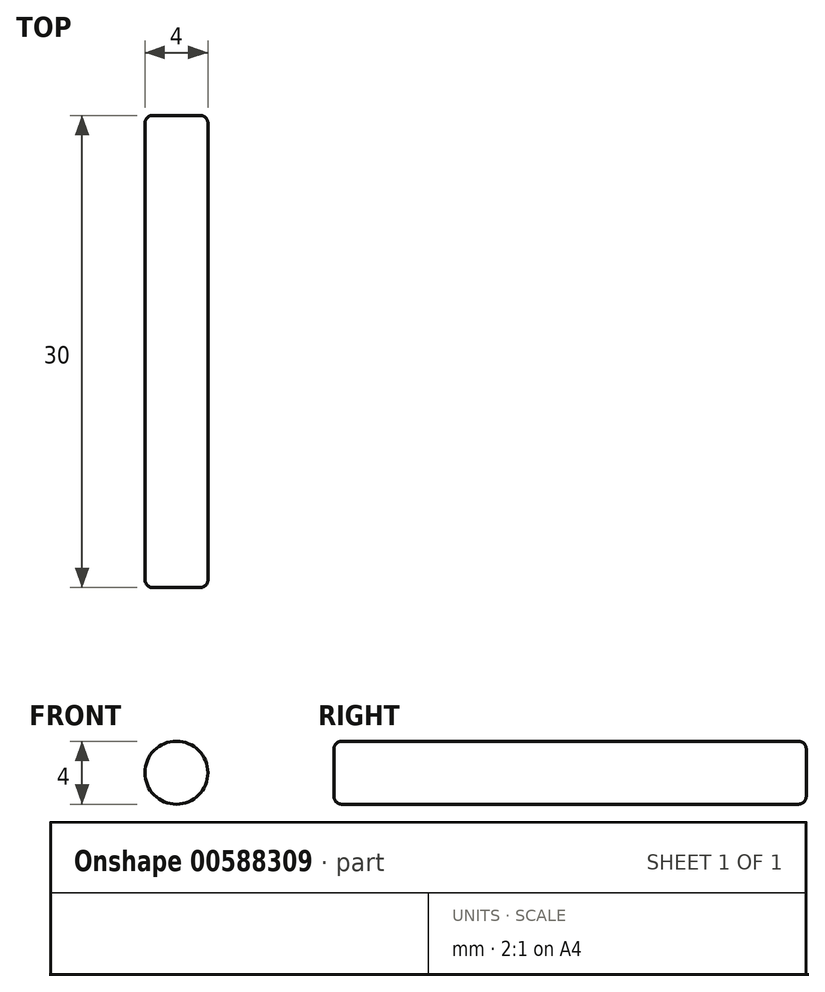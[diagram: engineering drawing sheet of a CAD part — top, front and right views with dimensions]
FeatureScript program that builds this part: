
annotation { "Feature Type Name" : "Feature", "Feature Type Description" : "" }
export const myFeature = defineFeature(function(context is Context, id is Id, definition is map)
    precondition{}
    {
        {
            var Q0;
            Q0=qCreatedBy(makeId("Right.planeOp"),FACE);
            var sketch = newSketch(context, id + "F0", { "sketchPlane" : qUnion([Q0])});
            skLineSegment(sketch, "E0", {"start": v(-95.37, 9.25) * mm, "end": v(-41.61, 9.25) * mm, "construction": true});
            skLineSegment(sketch, "E1", {"start": v(-26, 63) * mm, "end": v(-26, 16.75) * mm, "construction": true});
            skLineSegment(sketch, "E2", {"start": v(-15, 11.25) * mm, "end": v(-22.9, 11.25) * mm});
            skPoint(sketch, "E3.orphan", {"position": v(-26, 16.75) * mm});
            skLineSegment(sketch, "E4.MirrorCS", {"start": v(-37, 11.25) * mm, "end": v(-29.11, 11.25) * mm});
            skLineSegment(sketch, "E5", {"start": v(-29.11, 11.25) * mm, "end": v(-28.5, 11.25) * mm});
            skLineSegment(sketch, "E6", {"start": v(-23.5, 19.75) * mm, "end": v(-23.5, 11.25) * mm});
            skLineSegment(sketch, "E7", {"start": v(-23.5, 19.75) * mm, "end": v(-24, 19.75) * mm});
            skPoint(sketch, "E8.endSnap0", {"position": v(-25, 17.75) * mm});
            skLineSegment(sketch, "E9", {"start": v(-25, 17.75) * mm, "end": v(-25, 16.75) * mm});
            skLineSegment(sketch, "E10", {"start": v(-25, 16.75) * mm, "end": v(-26, 16.75) * mm});
            skLineSegment(sketch, "E11", {"start": v(-24, 19.75) * mm, "end": v(-24.5, 17.75) * mm});
            skLineSegment(sketch, "E12.trimOffspring", {"start": v(-24, 19.75) * mm, "end": v(-23.5, 19.75) * mm});
            skLineSegment(sketch, "E13", {"start": v(-28.5, 11.25) * mm, "end": v(-28.86, 11.25) * mm});
            skLineSegment(sketch, "E14.MirrorCS", {"start": v(-28, 19.75) * mm, "end": v(-28.5, 19.75) * mm});
            skLineSegment(sketch, "E15.MirrorCS", {"start": v(-28, 19.75) * mm, "end": v(-27.5, 17.75) * mm});
            skLineSegment(sketch, "E16.MirrorCS", {"start": v(-27, 17.75) * mm, "end": v(-27, 16.75) * mm});
            skLineSegment(sketch, "E17.MirrorCS", {"start": v(-27, 16.75) * mm, "end": v(-26, 16.75) * mm});
            skLineSegment(sketch, "E18", {"start": v(-27.5, 17.75) * mm, "end": v(-27, 17.75) * mm});
            skLineSegment(sketch, "E19", {"start": v(-25, 17.75) * mm, "end": v(-24.5, 17.75) * mm});
            skLineSegment(sketch, "E20.trimOffspring", {"start": v(-26, 11.25) * mm, "end": v(-26, -43.93) * mm, "construction": true});
            skPoint(sketch, "E21.orphan", {"position": v(-25, 16.75) * mm});
            skLineSegment(sketch, "E22.trimOffspring", {"start": v(-23.5, 11.25) * mm, "end": v(-22.9, 11.25) * mm});
            skPoint(sketch, "E23.orphan", {"position": v(-26, 19.75) * mm});
            skLineSegment(sketch, "E24", {"start": v(-41, 11.25) * mm, "end": v(-37, 11.25) * mm});
            skLineSegment(sketch, "E25", {"start": v(-11, 11.25) * mm, "end": v(-15, 11.25) * mm});
            skLineSegment(sketch, "E26.trimOffspring", {"start": v(-11, 9.25) * mm, "end": v(-97.5, 9.25) * mm, "construction": true});
            skLineSegment(sketch, "E27", {"start": v(-41.61, 9.25) * mm, "end": v(-11, 9.25) * mm});
            skLineSegment(sketch, "E28", {"start": v(-26, 9.25) * mm, "end": v(-41, 9.25) * mm});
            skLineSegment(sketch, "E29", {"start": v(-41, 9.25) * mm, "end": v(-41, 11.25) * mm});
            skLineSegment(sketch, "E30", {"start": v(-26, 9.25) * mm, "end": v(-11, 9.25) * mm});
            skLineSegment(sketch, "E31", {"start": v(-11, 9.25) * mm, "end": v(-11, 11.25) * mm});
            skPoint(sketch, "E32.orphan", {"position": v(-28.5, 9.25) * mm});
            skPoint(sketch, "E33.orphan", {"position": v(-23.5, 9.25) * mm});
            skLineSegment(sketch, "E34", {"start": v(-28.5, 11.25) * mm, "end": v(-23.5, 11.25) * mm});
            skSolve(sketch);
        }
        {
            var Q0;
            Q0=makeQuery(id+"F0.imprint","IMPRINT",FACE,{"disambiguationData":[TD([[makeQuery(id+"F0.imprint","IMPRINT",EDGE,{"derivedFrom":sQuery(id+"F0.wireOp",EDGE,"E2")}),1.0]])]});
            var Q1;
            Q1=sQuery(id+"F0.wireOp",EDGE,"E27");
            revolve(context, id + "F1", {"surfaceOperationType" : NewSurfaceOperationType.NEW, "entities" : qUnion([Q0]), "axis" : qUnion([Q1]), "revolveType" : RevolveType.FULL});
        }
        {
            var Q0;
            Q0=makeQuery(id+"F1.opRevolve","SWEPT_EDGE",EDGE,{"disambiguationData":[OSD([sQuery(id+"F0.wireOp",EDGE,"E24"),sQuery(id+"F0.wireOp",EDGE,"E29")])]});
            var Q1;
            Q1=makeQuery(id+"F1.opRevolve","SWEPT_EDGE",EDGE,{"disambiguationData":[OSD([sQuery(id+"F0.wireOp",EDGE,"E25"),sQuery(id+"F0.wireOp",EDGE,"E31")])]});
            fillet(context, id + "F2", {"entities" : qUnion([Q0, Q1]), "radius" : .5 * mm, "tangentPropagation" : true, "allowEdgeOverflow" : false});
        }
    });
